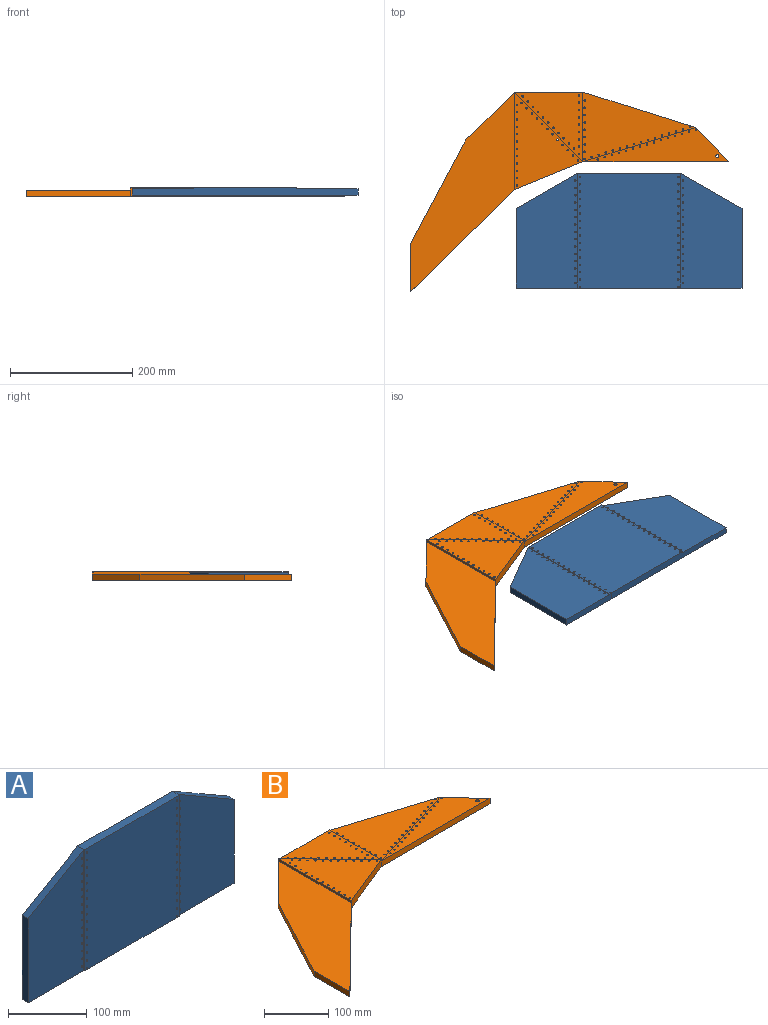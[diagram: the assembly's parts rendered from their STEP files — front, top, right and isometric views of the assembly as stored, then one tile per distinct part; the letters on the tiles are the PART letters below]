
ASSEMBLY  parts=2 mates=1
PART A: 74 faces, bbox 370x12x188 mm
  f0: plane 188x170mm, normal (0,-1,0), area 31790.1mm2, adj f2,f3,f4,f5,f28,f29,f30,f31
  f1: plane 370x188mm, normal (0,1,0), area 63457.3mm2, adj f2,f4,f6,f7,f9,f10,f12,f13
  f2: plane 170x12mm, normal (0,0,1), area 2040mm2, adj f0,f1,f3,f5,f6,f10
  f3: plane 188x1mm, normal (-1,0,0), area 188mm2, adj f0,f2,f4,f8
  f4: plane 370x12mm, normal (0,0,-1), area 4140mm2, adj f0,f1,f3,f5,f7,f8,f9,f11
  f5: plane 188x2mm, normal (1,0,0), area 376mm2, adj f0,f2,f4,f11
  f6: plane 100x57.74mm, normal (-0.5,0,0.87), area 1270.2mm2, adj f1,f2,f7,f8
  f7: plane 130.27x11mm, normal (-1,0,0), area 1432.9mm2, adj f1,f4,f6,f8
  f8: plane 188x100mm, normal (0,-1,0), area 15833.6mm2, adj f3,f4,f6,f7,f27,f57,f58,f59
  f9: plane 130.27x10mm, normal (1,0,0), area 1302.6mm2, adj f1,f4,f10,f11
  f10: plane 100x57.74mm, normal (0.5,0,0.87), area 1154.7mm2, adj f1,f2,f9,f11
  f11: plane 188x100mm, normal (0,-1,0), area 15833.6mm2, adj f4,f5,f9,f10,f12,f13,f14,f15
  f12: cylinder r=1.3mm len=10mm, axis (0,-1,0), area 81.7mm2, adj f1,f11
  f13: cylinder r=1.3mm len=10mm, axis (0,-1,0), area 81.7mm2, adj f1,f11
  f14: cylinder r=1.3mm len=10mm, axis (0,-1,0), area 81.7mm2, adj f1,f11
  f15: cylinder r=1.3mm len=10mm, axis (0,-1,0), area 81.7mm2, adj f1,f11
  f16: cylinder r=1.3mm len=10mm, axis (0,-1,0), area 81.7mm2, adj f1,f11
  f17: cylinder r=1.3mm len=10mm, axis (0,-1,0), area 81.7mm2, adj f1,f11
  f18: cylinder r=1.3mm len=10mm, axis (0,-1,0), area 81.7mm2, adj f1,f11
  f19: cylinder r=1.3mm len=10mm, axis (0,-1,0), area 81.7mm2, adj f1,f11
  f20: cylinder r=1.3mm len=10mm, axis (0,-1,0), area 81.7mm2, adj f1,f11
  f21: cylinder r=1.3mm len=10mm, axis (0,-1,0), area 81.7mm2, adj f1,f11
  f22: cylinder r=1.3mm len=10mm, axis (0,-1,0), area 81.7mm2, adj f1,f11
  f23: cylinder r=1.3mm len=10mm, axis (0,-1,0), area 81.7mm2, adj f1,f11
  f24: cylinder r=1.3mm len=10mm, axis (0,-1,0), area 81.7mm2, adj f1,f11
  f25: cylinder r=1.3mm len=10mm, axis (0,-1,0), area 81.7mm2, adj f1,f11
  f26: cylinder r=1.3mm len=10mm, axis (0,-1,0), area 81.7mm2, adj f1,f11
  f27: cylinder r=1.3mm len=11mm, axis (0,-1,0), area 89.8mm2, adj f1,f8
  f28: cylinder r=1.3mm len=12mm, axis (0,-1,0), area 98mm2, adj f0,f1
  f29: cylinder r=1.3mm len=12mm, axis (0,-1,0), area 98mm2, adj f0,f1
  f30: cylinder r=1.3mm len=12mm, axis (0,-1,0), area 98mm2, adj f0,f1
  f31: cylinder r=1.3mm len=12mm, axis (0,-1,0), area 98mm2, adj f0,f1
  f32: cylinder r=1.3mm len=12mm, axis (0,-1,0), area 98mm2, adj f0,f1
  f33: cylinder r=1.3mm len=12mm, axis (0,-1,0), area 98mm2, adj f0,f1
  f34: cylinder r=1.3mm len=12mm, axis (0,-1,0), area 98mm2, adj f0,f1
  f35: cylinder r=1.3mm len=12mm, axis (0,-1,0), area 98mm2, adj f0,f1
  f36: cylinder r=1.3mm len=12mm, axis (0,-1,0), area 98mm2, adj f0,f1
  f37: cylinder r=1.3mm len=12mm, axis (0,-1,0), area 98mm2, adj f0,f1
  f38: cylinder r=1.3mm len=12mm, axis (0,-1,0), area 98mm2, adj f0,f1
  f39: cylinder r=1.3mm len=12mm, axis (0,-1,0), area 98mm2, adj f0,f1
  f40: cylinder r=1.3mm len=12mm, axis (0,-1,0), area 98mm2, adj f0,f1
  f41: cylinder r=1.3mm len=12mm, axis (0,-1,0), area 98mm2, adj f0,f1
  f42: cylinder r=1.3mm len=12mm, axis (0,-1,0), area 98mm2, adj f0,f1
  f43: cylinder r=1.3mm len=12mm, axis (0,-1,0), area 98mm2, adj f0,f1
  f44: cylinder r=1.3mm len=12mm, axis (0,-1,0), area 98mm2, adj f0,f1
  f45: cylinder r=1.3mm len=12mm, axis (0,-1,0), area 98mm2, adj f0,f1
  f46: cylinder r=1.3mm len=12mm, axis (0,-1,0), area 98mm2, adj f0,f1
  f47: cylinder r=1.3mm len=12mm, axis (0,-1,0), area 98mm2, adj f0,f1
  f48: cylinder r=1.3mm len=12mm, axis (0,-1,0), area 98mm2, adj f0,f1
  f49: cylinder r=1.3mm len=12mm, axis (0,-1,0), area 98mm2, adj f0,f1
  f50: cylinder r=1.3mm len=12mm, axis (0,-1,0), area 98mm2, adj f0,f1
  f51: cylinder r=1.3mm len=12mm, axis (0,-1,0), area 98mm2, adj f0,f1
  f52: cylinder r=1.3mm len=12mm, axis (0,-1,0), area 98mm2, adj f0,f1
  f53: cylinder r=1.3mm len=12mm, axis (0,-1,0), area 98mm2, adj f0,f1
  f54: cylinder r=1.3mm len=12mm, axis (0,-1,0), area 98mm2, adj f0,f1
  f55: cylinder r=1.3mm len=12mm, axis (0,-1,0), area 98mm2, adj f0,f1
  f56: cylinder r=1.3mm len=12mm, axis (0,-1,0), area 98mm2, adj f0,f1
  f57: cylinder r=1.3mm len=11mm, axis (0,-1,0), area 89.8mm2, adj f1,f8
  f58: cylinder r=1.3mm len=11mm, axis (0,-1,0), area 89.8mm2, adj f1,f8
  f59: cylinder r=1.3mm len=11mm, axis (0,-1,0), area 89.8mm2, adj f1,f8
  f60: cylinder r=1.3mm len=11mm, axis (0,-1,0), area 89.8mm2, adj f1,f8
  f61: cylinder r=1.3mm len=11mm, axis (0,-1,0), area 89.8mm2, adj f1,f8
  f62: cylinder r=1.3mm len=11mm, axis (0,-1,0), area 89.8mm2, adj f1,f8
  f63: cylinder r=1.3mm len=11mm, axis (0,-1,0), area 89.8mm2, adj f1,f8
  f64: cylinder r=1.3mm len=11mm, axis (0,-1,0), area 89.8mm2, adj f1,f8
  f65: cylinder r=1.3mm len=11mm, axis (0,-1,0), area 89.8mm2, adj f1,f8
  f66: cylinder r=1.3mm len=11mm, axis (0,-1,0), area 89.8mm2, adj f1,f8
  f67: cylinder r=1.3mm len=11mm, axis (0,-1,0), area 89.8mm2, adj f1,f8
  f68: cylinder r=1.3mm len=11mm, axis (0,-1,0), area 89.8mm2, adj f1,f8
  f69: cylinder r=1.3mm len=11mm, axis (0,-1,0), area 89.8mm2, adj f1,f8
  f70: cylinder r=1.3mm len=11mm, axis (0,-1,0), area 89.8mm2, adj f1,f8
  f71: cylinder r=1.3mm len=12mm, axis (0,-1,0), area 98mm2, adj f0,f1
  f72: cylinder r=1.3mm len=12mm, axis (0,-1,0), area 98mm2, adj f0,f1
  f73: cylinder r=1.3mm len=12mm, axis (0,-1,0), area 98mm2, adj f0,f1
PART B: 103 faces, bbox 522x327.3x14 mm
  f0: plane 159.81x112mm, normal (0,0,1), area 8822.1mm2, adj f11,f12,f13,f20,f21,f22,f23,f24
  f1: plane 521.99x327.31mm, normal (0,0,-1), area 55693.3mm2, adj f2,f3,f6,f9,f13,f15,f16,f17
  f2: plane 239x11mm, normal (0,-1,0), area 2629mm2, adj f1,f3,f4,f13
  f3: plane 55.99x54.3mm, normal (0.72,0.7,0), area 858mm2, adj f1,f2,f4,f6
  f4: plane 239x55.99mm, normal (0,0,1), area 6589.8mm2, adj f2,f3,f5,f56,f71,f72,f73,f74
  f5: plane 184.7x55.99mm, normal (0.29,-0.96,0), area 193mm2, adj f4,f6,f7,f13
  f6: plane 184.7x58.01mm, normal (0.3,0.95,0), area 2323.1mm2, adj f1,f3,f5,f7,f9
  f7: plane 184.7x114mm, normal (0,0,1), area 10400.4mm2, adj f5,f6,f8,f40,f41,f42,f47,f48
  f8: plane 114x1mm, normal (1,0,0), area 114mm2, adj f7,f9,f10,f13
  f9: plane 112x13mm, normal (0,1,0), area 1456mm2, adj f1,f6,f8,f10,f12,f15
  f10: plane 114x112mm, normal (0,0,1), area 6277.8mm2, adj f8,f9,f11,f19,f39,f43,f44,f45
  f11: plane 114x112mm, normal (0.71,0.7,0), area 159.8mm2, adj f0,f10,f12,f13
  f12: plane 159.81x4mm, normal (-1,0,0), area 639.2mm2, adj f0,f9,f11,f13,f14
  f13: plane 112x45.81mm, normal (0.38,-0.93,0), area 1694.1mm2, adj f0,f1,f2,f5,f8,f11,f12,f18
  f14: plane 327.31x170.99mm, normal (0,0,1), area 23603.2mm2, adj f12,f15,f16,f17,f18
  f15: plane 79.89x78.49mm, normal (-0.7,0.71,0), area 1120mm2, adj f1,f9,f14,f16
  f16: plane 170.82x91.1mm, normal (-0.88,0.47,0), area 1935.9mm2, adj f1,f14,f15,f17
  f17: plane 78x10mm, normal (-1,-0.01,0), area 780mm2, adj f1,f14,f16,f18
  f18: plane 170.49x167.5mm, normal (0.7,-0.71,0), area 2390mm2, adj f1,f13,f14,f17
  f19: cylinder r=1.3mm len=13mm, axis (0,0,1), area 106.2mm2, adj f1,f10
  f20: cylinder r=1.3mm len=14mm, axis (0,0,1), area 114.4mm2, adj f0,f1
  f21: cylinder r=1.3mm len=14mm, axis (0,0,1), area 114.4mm2, adj f0,f1
  f22: cylinder r=1.3mm len=14mm, axis (0,0,1), area 114.4mm2, adj f0,f1
  f23: cylinder r=1.3mm len=14mm, axis (0,0,1), area 114.4mm2, adj f0,f1
  f24: cylinder r=1.3mm len=14mm, axis (0,0,1), area 114.4mm2, adj f0,f1
  f25: cylinder r=1.3mm len=14mm, axis (0,0,1), area 114.4mm2, adj f0,f1
  f26: cylinder r=1.3mm len=14mm, axis (0,0,1), area 114.4mm2, adj f0,f1
  f27: cylinder r=1.3mm len=14mm, axis (0,0,1), area 114.4mm2, adj f0,f1
  f28: cylinder r=1.3mm len=14mm, axis (0,0,1), area 114.4mm2, adj f0,f1
  f29: cylinder r=1.3mm len=14mm, axis (0,0,1), area 114.4mm2, adj f0,f1
  f30: cylinder r=1.3mm len=14mm, axis (0,0,1), area 114.4mm2, adj f0,f1
  f31: cylinder r=1.3mm len=14mm, axis (0,0,1), area 114.4mm2, adj f0,f1
  f32: cylinder r=1.3mm len=14mm, axis (0,0,1), area 114.4mm2, adj f0,f1
  f33: cylinder r=1.3mm len=14mm, axis (0,0,1), area 114.4mm2, adj f0,f1
  f34: cylinder r=1.3mm len=14mm, axis (0,0,1), area 114.4mm2, adj f0,f1
  f35: cylinder r=1.3mm len=14mm, axis (0,0,1), area 114.4mm2, adj f0,f1
  f36: cylinder r=1.3mm len=14mm, axis (0,0,1), area 114.4mm2, adj f0,f1
  f37: cylinder r=1.3mm len=14mm, axis (0,0,1), area 114.4mm2, adj f0,f1
  f38: cylinder r=1.3mm len=14mm, axis (0,0,1), area 114.4mm2, adj f0,f1
  f39: cylinder r=1.3mm len=13mm, axis (0,0,1), area 106.2mm2, adj f1,f10
  f40: cylinder r=1.3mm len=12mm, axis (0,0,1), area 98mm2, adj f1,f7
  f41: cylinder r=1.3mm len=12mm, axis (0,0,1), area 98mm2, adj f1,f7
  f42: cylinder r=1.3mm len=12mm, axis (0,0,1), area 98mm2, adj f1,f7
  f43: cylinder r=1.3mm len=13mm, axis (0,0,1), area 106.2mm2, adj f1,f10
  f44: cylinder r=1.3mm len=13mm, axis (0,0,1), area 106.2mm2, adj f1,f10
  f45: cylinder r=1.3mm len=13mm, axis (0,0,1), area 106.2mm2, adj f1,f10
  f46: cylinder r=1.3mm len=13mm, axis (0,0,1), area 106.2mm2, adj f1,f10
  f47: cylinder r=1.3mm len=12mm, axis (0,0,1), area 98mm2, adj f1,f7
  f48: cylinder r=1.3mm len=12mm, axis (0,0,1), area 98mm2, adj f1,f7
  f49: cylinder r=1.3mm len=12mm, axis (0,0,1), area 98mm2, adj f1,f7
  f50: cylinder r=1.3mm len=12mm, axis (0,0,1), area 98mm2, adj f1,f7
  f51: cylinder r=1.3mm len=12mm, axis (0,0,1), area 98mm2, adj f1,f7
  f52: cylinder r=1.3mm len=12mm, axis (0,0,1), area 98mm2, adj f1,f7
  f53: cylinder r=1.3mm len=12mm, axis (0,0,1), area 98mm2, adj f1,f7
  f54: cylinder r=1.3mm len=12mm, axis (0,0,1), area 98mm2, adj f1,f7
  f55: cylinder r=1.3mm len=12mm, axis (0,0,1), area 98mm2, adj f1,f7
  f56: cylinder r=1.3mm len=11mm, axis (0,0,1), area 89.8mm2, adj f1,f4
  f57: cylinder r=1.3mm len=13mm, axis (0,0,1), area 106.2mm2, adj f1,f10
  f58: cylinder r=1.3mm len=13mm, axis (0,0,1), area 106.2mm2, adj f1,f10
  f59: cylinder r=1.3mm len=13mm, axis (0,0,1), area 106.2mm2, adj f1,f10
  f60: cylinder r=1.3mm len=13mm, axis (0,0,1), area 106.2mm2, adj f1,f10
  f61: cylinder r=1.3mm len=13mm, axis (0,0,1), area 106.2mm2, adj f1,f10
  f62: cylinder r=1.3mm len=13mm, axis (0,0,1), area 106.2mm2, adj f1,f10
  f63: cylinder r=1.3mm len=13mm, axis (0,0,1), area 106.2mm2, adj f1,f10
  f64: cylinder r=1.3mm len=13mm, axis (0,0,1), area 106.2mm2, adj f1,f10
  f65: cylinder r=1.3mm len=13mm, axis (0,0,1), area 106.2mm2, adj f1,f10
  f66: cylinder r=1.3mm len=13mm, axis (0,0,1), area 106.2mm2, adj f1,f10
  f67: cylinder r=1.3mm len=13mm, axis (0,0,1), area 106.2mm2, adj f1,f10
  f68: cylinder r=1.3mm len=13mm, axis (0,0,1), area 106.2mm2, adj f1,f10
  f69: cylinder r=1.3mm len=13mm, axis (0,0,1), area 106.2mm2, adj f1,f10
  f70: cylinder r=1.3mm len=13mm, axis (0,0,1), area 106.2mm2, adj f1,f10
  f71: cylinder r=1.3mm len=11mm, axis (0,0,1), area 89.8mm2, adj f1,f4
  f72: cylinder r=1.3mm len=11mm, axis (0,0,1), area 89.8mm2, adj f1,f4
  f73: cylinder r=1.3mm len=11mm, axis (0,0,1), area 89.8mm2, adj f1,f4
  f74: cylinder r=1.3mm len=11mm, axis (0,0,1), area 89.8mm2, adj f1,f4
  f75: cylinder r=1.3mm len=11mm, axis (0,0,1), area 89.8mm2, adj f1,f4
  f76: cylinder r=1.3mm len=11mm, axis (0,0,1), area 89.8mm2, adj f1,f4
  f77: cylinder r=1.3mm len=11mm, axis (0,0,1), area 89.8mm2, adj f1,f4
  f78: cylinder r=1.3mm len=11mm, axis (0,0,1), area 89.8mm2, adj f1,f4
  f79: cylinder r=1.3mm len=11mm, axis (0,0,1), area 89.8mm2, adj f1,f4
  f80: cylinder r=2.64mm len=11mm, axis (0,0,1), area 182.3mm2, adj f1,f4
  f81: cylinder r=1.3mm len=12mm, axis (0,0,1), area 98mm2, adj f1,f7
  f82: cylinder r=1.3mm len=14mm, axis (0,0,1), area 114.4mm2, adj f0,f1
  f83: cylinder r=1.3mm len=14mm, axis (0,0,1), area 114.4mm2, adj f0,f1
  f84: cylinder r=1.3mm len=14mm, axis (0,0,1), area 114.4mm2, adj f0,f1
  f85: cylinder r=1.3mm len=14mm, axis (0,0,1), area 114.4mm2, adj f0,f1
  f86: cylinder r=1.3mm len=14mm, axis (0,0,1), area 114.4mm2, adj f0,f1
  f87: cylinder r=1.3mm len=12mm, axis (0,0,1), area 98mm2, adj f1,f7
  f88: cylinder r=1.3mm len=12mm, axis (0,0,1), area 98mm2, adj f1,f7
  f89: cylinder r=1.3mm len=12mm, axis (0,0,1), area 98mm2, adj f1,f7
  f90: cylinder r=1.3mm len=12mm, axis (0,0,1), area 98mm2, adj f1,f7
  f91: cylinder r=1.3mm len=12mm, axis (0,0,1), area 98mm2, adj f1,f7
  f92: cylinder r=1.3mm len=12mm, axis (0,0,1), area 98mm2, adj f1,f7
  f93: cylinder r=1.3mm len=12mm, axis (0,0,1), area 98mm2, adj f1,f7
  f94: cylinder r=1.3mm len=12mm, axis (0,0,1), area 98mm2, adj f1,f7
  f95: cylinder r=1.3mm len=11mm, axis (0,0,1), area 89.8mm2, adj f1,f4
  f96: cylinder r=1.3mm len=11mm, axis (0,0,1), area 89.8mm2, adj f1,f4
  f97: cylinder r=1.3mm len=11mm, axis (0,0,1), area 89.8mm2, adj f1,f4
  f98: cylinder r=1.3mm len=11mm, axis (0,0,1), area 89.8mm2, adj f1,f4
  f99: cylinder r=1.3mm len=12mm, axis (0,0,1), area 98mm2, adj f1,f7
  f100: cylinder r=1.3mm len=12mm, axis (0,0,1), area 98mm2, adj f1,f7
  f101: cylinder r=1.3mm len=12mm, axis (0,0,1), area 98mm2, adj f1,f7
  f102: cylinder r=1.3mm len=11mm, axis (0,0,1), area 89.8mm2, adj f1,f4
PLACE A rot(axis=(-1,0,0),90deg) t=(9,-176.86,80.3)mm
PLACE B t=(-94.88,-82.28,78.3)mm fixed
MATE planar A.f0 <-> B.f0  axis (0,0,1) through (-104.18,-195.21,82.3)mm
